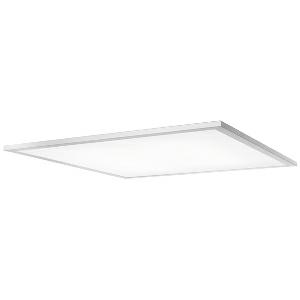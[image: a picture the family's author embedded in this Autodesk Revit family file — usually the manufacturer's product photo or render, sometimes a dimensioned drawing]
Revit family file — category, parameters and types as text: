
# Revit family: dotoo_fit_-_dfe_4000_840_sm625_00808115_36a6
name_source: partatom
category: Lighting Fixtures
units: mm (PartAtom-declared; Revit-internal decimal feet)

## family parameters
Cut with Voids When Loaded = No
Host = Face
Light Source = No
Part Type = Normal
Room Calculation Point = No
Round Connector Dimension = Use Diameter
Shared = No

## types (1)
- DOTOO.fit - DFE 4000/840 SM625 (1 x LED, 4100 lm, 4000K)
    Apparent Load = 30 VA
    Approval mark = CE
    CIE Flux Codes = 66 90 98 100 100
    Color Rendering = 80-89
    Color Temperature = 4000K
    Control Gear = Electronic ballast
    Default Elevation = 1800 mm
    Description = DFE 4000/840|Recessed modular luminaire|light source:  |work equipment: Electronic ballast|connected load: 220-240 V, 50/60 Hz|Power consumption: approx. 30 W|standby: approx. 0,50|power factor: approx. 0,900|luminous flux: 4100 lm|luminous efficacy: 136 lm/W|light distribution: Direct|direct ratio: approx. 100 %|colour temperature: Cold white, ca. 4000 K|color rendering index (CRI): >= 80|chromaticity tolerance:  3 SDCM|System of protection: IP 20|class of protection: II|technology: Switchable|operation: External|luminaire body|material: Sectional aluminium|colour: White|weight (net): approx. 3.0 kg|mains lead: 0.50 m Connector|glare control: Prism aperture|luminance(L65): <= 2700 cd/m|unified glare rating(4H 8H): <=  19|special features: Direct light component with edge light and light-guide technology for homogenous light exit, Flicker-free, System dimension 625 x 625 mm, Strain relief with the possibility of through-wiring|
    Height = 0 mm  [stored 0 ft]
    Lamp = 1 x LED
    Lamp Light Flux = 4100 lm
    Lamp count = 1
    Length = 622 mm
    Luminous efficacy = 137 lm/W
    Manufacturer = Waldmann
    ModVariant = No
    Model = 00808115
    Mounting Place = Ceiling
    Mounting Type = Recessed
    Number of Poles = 1
    OnlyDefault = Yes
    Power Factor = 1
    Product Name = DOTOO.fit - DFE 4000/840 SM625
    Product group = Recessed luminaire
    ProductGroupID = 4
    Protection Class = Protection class II
    Protection Degree = IP 20
    RLX_Detail_Level = 1
    RLX_Emergency_Light_Flux = 0 lm
    RLX_Emergency_Type = 0
    RLX_Emergency_Type_DB = No
    RlxData = <blob elided: 37533 chars, md5=b422fd82>
    Socket = socket
    Standby Power = 0 W
    System Light Flux = 4100 lm
    System Power = 30 W
    Type Comments = Product without accessories
    Type Image = 113328000-00692486.jpg
    URL = http://relux.com
    VarID = ---
    Voltage = 230 V
    Voltage Range = 220-240 V
    Weight = 0.00 kg
    Width = 622 mm

note: [stored X ft] marks values corroborated as IEEE doubles in the binary element streams (Revit-internal decimal feet)

## geometry (parser evidence)
native form markers: Blend x4, Sweep x11
no freeform markers — native parametric forms only
